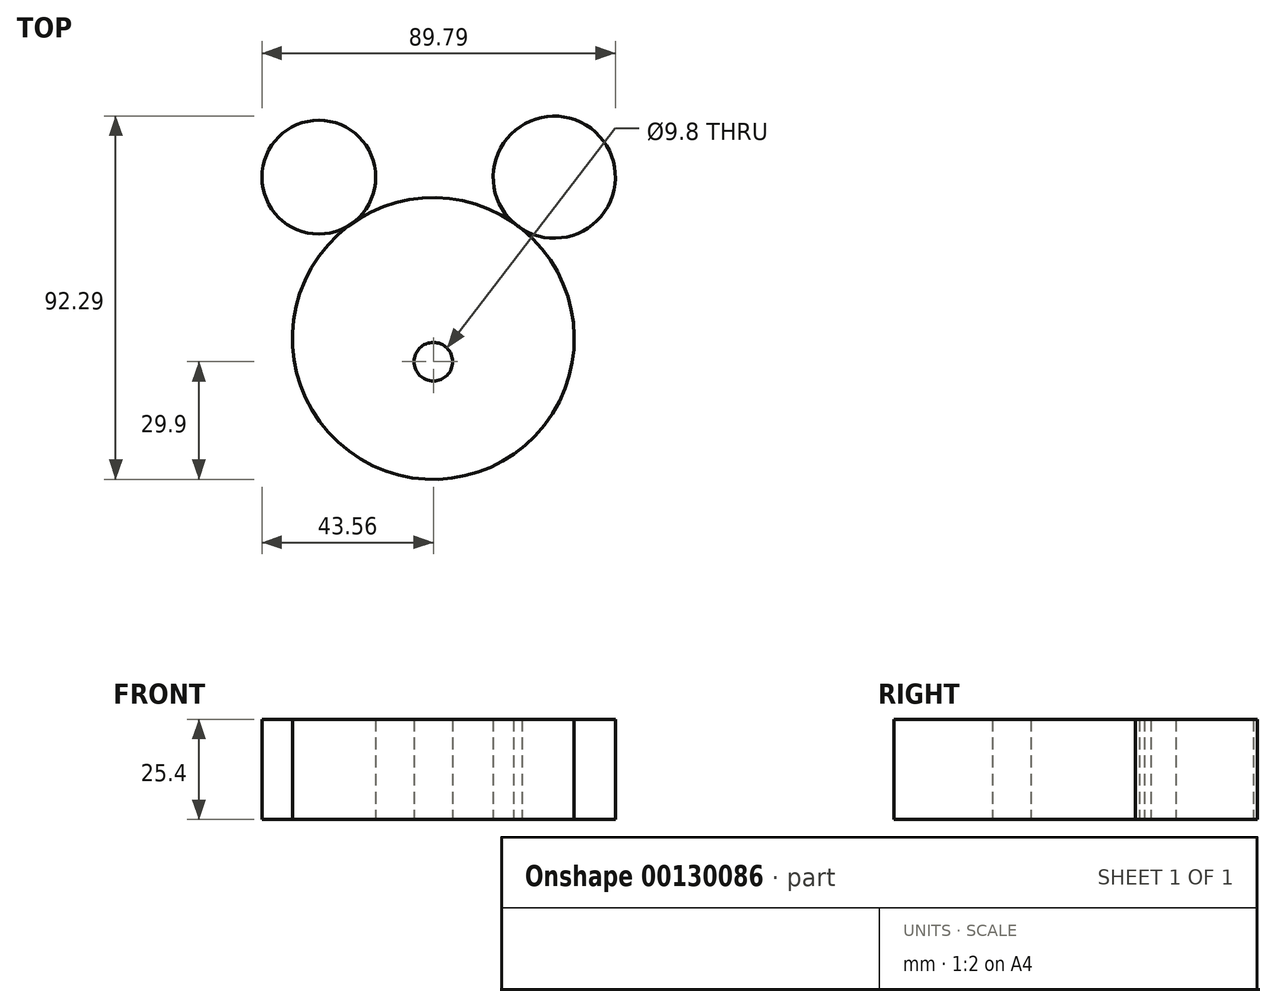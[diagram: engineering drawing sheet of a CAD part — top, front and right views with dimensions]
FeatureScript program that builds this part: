
annotation { "Feature Type Name" : "Feature", "Feature Type Description" : "" }
export const myFeature = defineFeature(function(context is Context, id is Id, definition is map)
    precondition{}
    {
        {
            var Q0;
            Q0=qCreatedBy(makeId("Top.planeOp"),FACE);
            var sketch = newSketch(context, id + "F0", { "sketchPlane" : qUnion([Q0])});
            skCircle(sketch, "E0", {"center": v(0, 0) * mm, "radius": 35.8 * mm});
            skCircle(sketch, "E1", {"center": v(-29.1, 40.99) * mm, "radius": 14.47 * mm});
            skCircle(sketch, "E2", {"center": v(30.71, 40.99) * mm, "radius": 15.51 * mm});
            skCircle(sketch, "E3", {"center": v(0, -5.9) * mm, "radius": 4.9 * mm});
            skSolve(sketch);
        }
        {
            var Q0;
            Q0=makeQuery(id+"F0.imprint","IMPRINT",FACE,{"disambiguationData":[TD([[makeQuery(id+"F0.imprint","IMPRINT",EDGE,{"derivedFrom":sQuery(id+"F0.wireOp",EDGE,"E3")}),-1.0]])]});
            var Q1;
            Q1=makeQuery(id+"F0.imprint","IMPRINT",FACE,{"disambiguationData":[TD([[makeQuery(id+"F0.imprint","IMPRINT",EDGE,{"derivedFrom":sQuery(id+"F0.wireOp",EDGE,"E1")}),1.0]])]});
            var Q2;
            {var subQ0=sQuery(id+"F0.wireOp",EDGE,"E2");var subQ1=sQuery(id+"F0.wireOp",EDGE,"E0");var subQ2=makeQuery(id+"F0.imprint","INTERSECT",VERTEX,{"disambiguationData":[OD(0.0)],"derivedFrom":[subQ1,subQ0]});Q2=makeQuery(id+"F0.imprint","IMPRINT",FACE,{"disambiguationData":[TD([[makeQuery(id+"F0.imprint","IMPRINT",EDGE,{"disambiguationData":[TD([[subQ2,1.0]])],"derivedFrom":subQ1}),-1.0]])]});}
            extrude(context, id + "F1", {"entities" : qUnion([Q0, Q1, Q2]), "depth" : 25.4 * mm});
        }
        {
            var Q0;
            Q0=qCreatedBy(makeId("Top.planeOp"),FACE);
            var sketch = newSketch(context, id + "F2", { "sketchPlane" : qUnion([Q0])});
            skCircle(sketch, "E4", {"center": v(-13.16, 16.74) * mm, "radius": 9.54 * mm});
            skCircle(sketch, "E5", {"center": v(12, 17.43) * mm, "radius": 9.15 * mm});
            skSolve(sketch);
        }
        {
            var Q0;
            Q0=sQuery(id+"F2.wireOp",EDGE,"E4");
            extrude(context, id + "F3", {"bodyType" : ToolBodyType.SURFACE, "surfaceEntities" : qUnion([Q0]), "oppositeDirection" : true, "depth" : 28.7 * mm});
        }
    });
